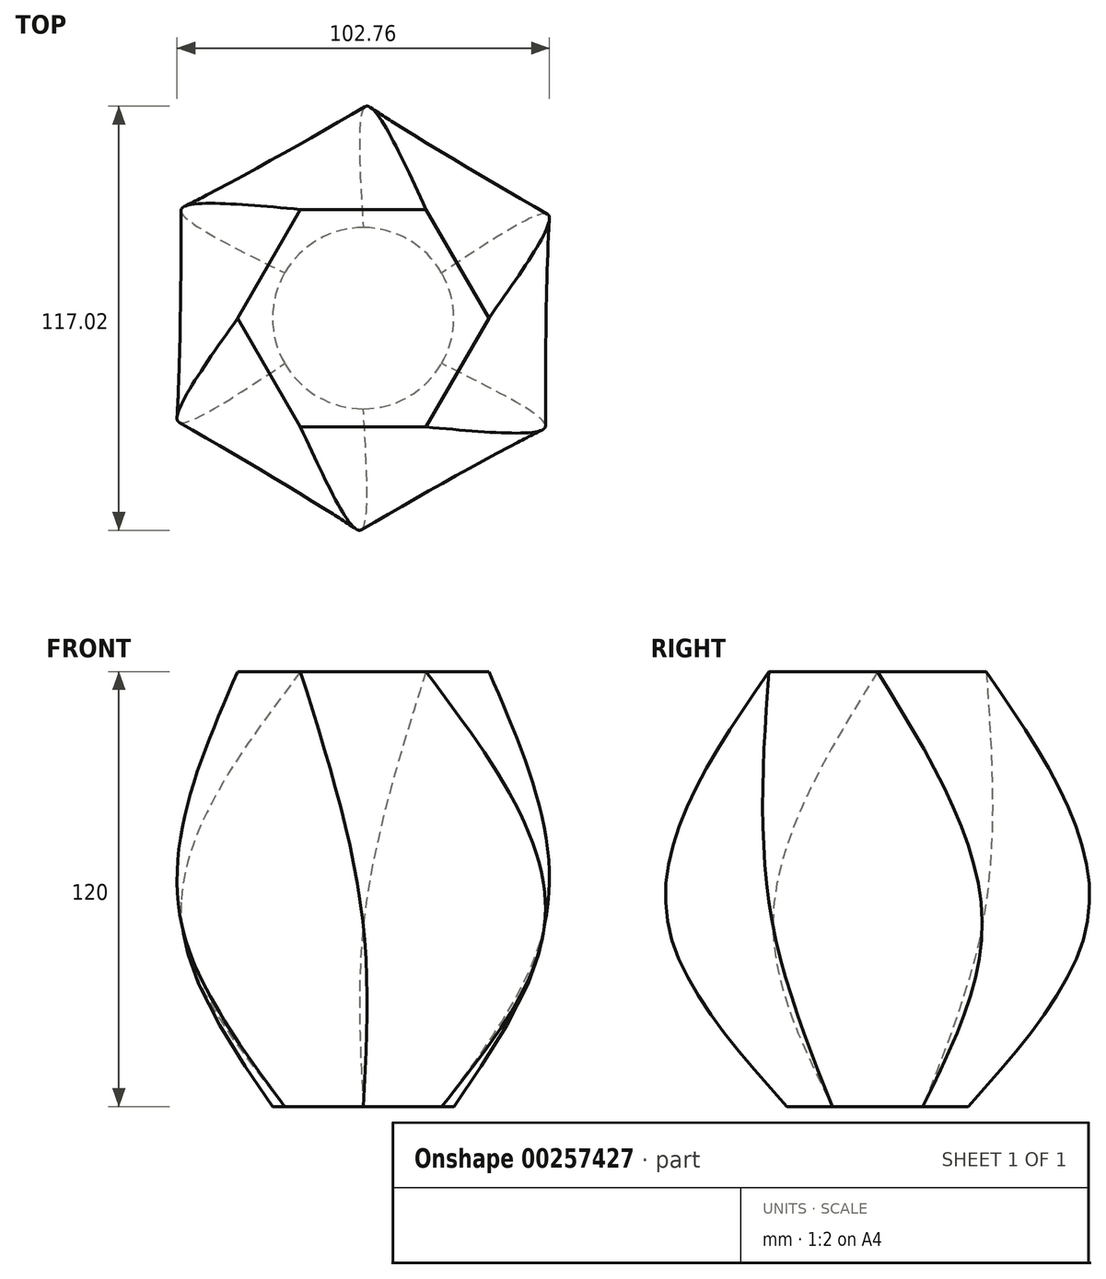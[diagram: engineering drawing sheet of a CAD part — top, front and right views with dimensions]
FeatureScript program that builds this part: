
annotation { "Feature Type Name" : "Feature", "Feature Type Description" : "" }
export const myFeature = defineFeature(function(context is Context, id is Id, definition is map)
    precondition{}
    {
        {
            var Q0;
            Q0=qCreatedBy(makeId("Top.planeOp"),FACE);
            var sketch = newSketch(context, id + "F0", { "sketchPlane" : qUnion([Q0])});
            skCircle(sketch, "E0.cCircle", {"center": v(0, 0) * mm, "radius": 30 * mm, "construction": true});
            skLineSegment(sketch, "E0.0", {"start": v(17.32, -30) * mm, "end": v(-17.32, -30) * mm});
            skLineSegment(sketch, "E0.1", {"start": v(-17.32, -30) * mm, "end": v(-34.64, 0) * mm});
            skLineSegment(sketch, "E0.2", {"start": v(-34.64, 0) * mm, "end": v(-17.32, 30) * mm});
            skLineSegment(sketch, "E0.3", {"start": v(-17.32, 30) * mm, "end": v(17.32, 30) * mm});
            skLineSegment(sketch, "E0.4", {"start": v(17.32, 30) * mm, "end": v(34.64, 0) * mm});
            skLineSegment(sketch, "E0.5", {"start": v(34.64, 0) * mm, "end": v(17.32, -30) * mm});
            skPoint(sketch, "E0.0.midPoint", {"position": v(0, -30) * mm});
            skSolve(sketch);
        }
        {
            var Q0;
            Q0=qCreatedBy(makeId("Top.planeOp"),FACE);
            cPlane(context, id + "F1", {"entities" : qUnion([Q0]), "cplaneType" : CPlaneType.OFFSET, "offset" : 70 * mm, "oppositeDirection" : true, "width" : 150 * mm, "height" : 150 * mm});
        }
        {
            var Q0;
            Q0=qCreatedBy(id+"F1.planeOp",FACE);
            var sketch = newSketch(context, id + "F2", { "sketchPlane" : qUnion([Q0])});
            skCircle(sketch, "E1.cCircle", {"center": v(0, 0) * mm, "radius": 50 * mm, "construction": true});
            skLineSegment(sketch, "E1.0", {"start": v(50, -28.87) * mm, "end": v(0, -57.74) * mm});
            skLineSegment(sketch, "E1.1", {"start": v(0, -57.74) * mm, "end": v(-50, -28.86) * mm});
            skLineSegment(sketch, "E1.2", {"start": v(-50, -28.86) * mm, "end": v(-50, 28.87) * mm});
            skLineSegment(sketch, "E1.3", {"start": v(-50, 28.87) * mm, "end": v(0, 57.74) * mm});
            skLineSegment(sketch, "E1.4", {"start": v(0, 57.74) * mm, "end": v(50, 28.86) * mm});
            skLineSegment(sketch, "E1.5", {"start": v(50, 28.86) * mm, "end": v(50, -28.87) * mm});
            skPoint(sketch, "E1.0.midPoint", {"position": v(25, -43.3) * mm});
            skSolve(sketch);
        }
        {
            var Q0;
            Q0=qCreatedBy(id+"F1.planeOp",FACE);
            cPlane(context, id + "F3", {"entities" : qUnion([Q0]), "cplaneType" : CPlaneType.OFFSET, "offset" : 50 * mm, "oppositeDirection" : true, "width" : 150 * mm, "height" : 150 * mm});
        }
        {
            var Q0;
            Q0=qCreatedBy(id+"F3.planeOp",FACE);
            var sketch = newSketch(context, id + "F4", { "sketchPlane" : qUnion([Q0])});
            skCircle(sketch, "E2", {"center": v(0, 0) * mm, "radius": 25 * mm});
            skSolve(sketch);
        }
        {
            var Q0;
            Q0=makeQuery(id+"F0.imprint","IMPRINT",FACE,{"disambiguationData":[TD([[makeQuery(id+"F0.imprint","IMPRINT",EDGE,{"derivedFrom":sQuery(id+"F0.wireOp",EDGE,"E0.0")}),-1.0]])]});
            var Q1;
            Q1=makeQuery(id+"F2.imprint","IMPRINT",FACE,{"disambiguationData":[TD([[makeQuery(id+"F2.imprint","IMPRINT",EDGE,{"derivedFrom":sQuery(id+"F2.wireOp",EDGE,"E1.0")}),-1.0]])]});
            var Q2;
            Q2=makeQuery(id+"F4.imprint","IMPRINT",FACE,{"disambiguationData":[TD([[makeQuery(id+"F4.imprint","IMPRINT",EDGE,{"derivedFrom":sQuery(id+"F4.wireOp",EDGE,"E2")}),1.0]])]});
            loft(context, id + "F5", {"sheetProfilesArray" : [{ "sheetProfileEntities" : qUnion([Q0]) }, { "sheetProfileEntities" : qUnion([Q1]) }, { "sheetProfileEntities" : qUnion([Q2]) }]});
        }
    });
